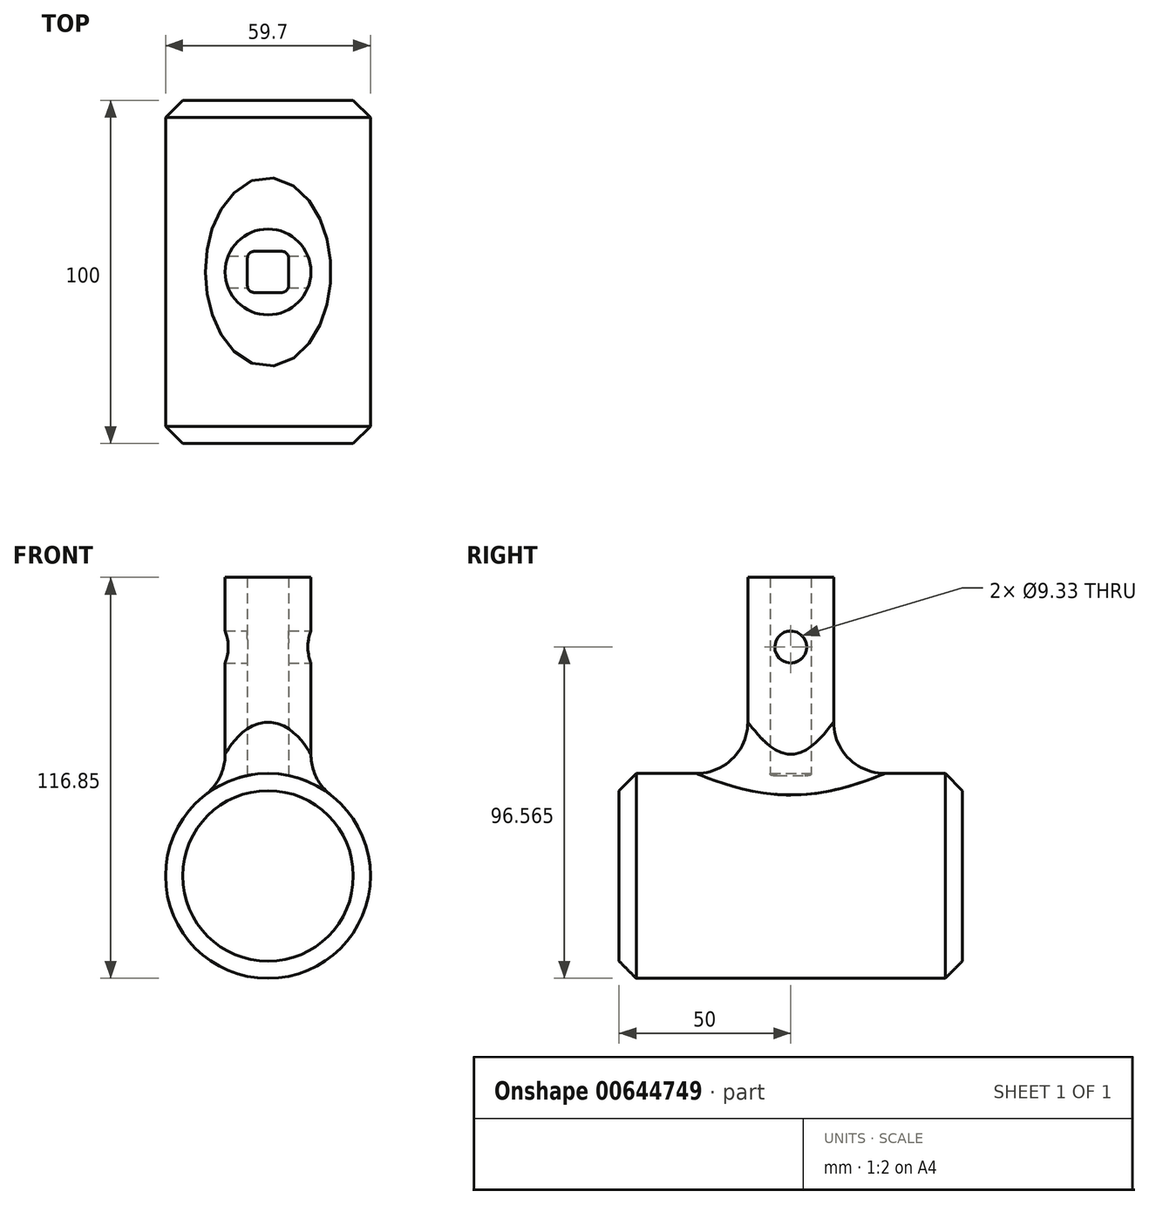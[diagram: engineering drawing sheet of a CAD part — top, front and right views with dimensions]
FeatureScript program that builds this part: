
annotation { "Feature Type Name" : "Feature", "Feature Type Description" : "" }
export const myFeature = defineFeature(function(context is Context, id is Id, definition is map)
    precondition{}
    {
        {
            var Q0;
            Q0=qCreatedBy(makeId("Top.planeOp"),FACE);
            var sketch = newSketch(context, id + "F0", { "sketchPlane" : qUnion([Q0])});
            skCircle(sketch, "E0", {"center": v(0, 0) * mm, "radius": 12.5 * mm});
            skLineSegment(sketch, "E1.bottom", {"start": v(4, -6) * mm, "end": v(-4, -6) * mm});
            skLineSegment(sketch, "E1.top", {"start": v(4, 6) * mm, "end": v(-4, 6) * mm});
            skLineSegment(sketch, "E1.left", {"start": v(6, -4) * mm, "end": v(6, 4) * mm});
            skLineSegment(sketch, "E1.right", {"start": v(-6, -4) * mm, "end": v(-6, 4) * mm});
            skPoint(sketch, "E2.visualSharp", {"position": v(-6, 6) * mm});
            skArc(sketch, "E2.filletArc", {"start": v(-4, 6) * mm, "mid": v(-5.41, 5.41) * mm, "end": v(-6, 4) * mm});
            skPoint(sketch, "E3.visualSharp", {"position": v(-6, -6) * mm});
            skArc(sketch, "E3.filletArc", {"start": v(-6, -4) * mm, "mid": v(-5.41, -5.41) * mm, "end": v(-4, -6) * mm});
            skPoint(sketch, "E4.visualSharp", {"position": v(6, -6) * mm});
            skArc(sketch, "E4.filletArc", {"start": v(4, -6) * mm, "mid": v(5.41, -5.41) * mm, "end": v(6, -4) * mm});
            skPoint(sketch, "E5.visualSharp", {"position": v(6, 6) * mm});
            skArc(sketch, "E5.filletArc", {"start": v(6, 4) * mm, "mid": v(5.41, 5.41) * mm, "end": v(4, 6) * mm});
            skSolve(sketch);
        }
        {
            var Q0;
            Q0 = qSketchRegion(id + "F0", true);
            extrude(context, id + "F1", {"entities" : qUnion([Q0]), "depth" : 87 * mm, "offsetDistance" : 25 * mm});
        }
        {
            var Q0;
            Q0=qCreatedBy(makeId("Front.planeOp"),FACE);
            var sketch = newSketch(context, id + "F2", { "sketchPlane" : qUnion([Q0])});
            skCircle(sketch, "E6", {"center": v(0, 0) * mm, "radius": 29.85 * mm});
            skSolve(sketch);
        }
        {
            var Q0;
            Q0 = qSketchRegion(id + "F2", true);
            extrude(context, id + "F3", {"entities" : qUnion([Q0]), "operationType" : NewBodyOperationType.ADD, "endBound" : BoundingType.SYMMETRIC, "depth" : 100 * mm, "offsetDistance" : 25 * mm});
        }
        {
            var Q0;
            Q0=makeQuery(id+"F3.boolean.opBoolean","INTERSECT",EDGE,{"derivedFrom":[makeQuery(id+"F1.opExtrude","SWEPT_FACE",FACE,{"disambiguationData":[OSD([sQuery(id+"F0.wireOp",EDGE,"E0")])]}),makeQuery(id+"F3.opExtrude","SWEPT_FACE",FACE,{"disambiguationData":[OSD([sQuery(id+"F2.wireOp",EDGE,"E6")])]})]});
            fillet(context, id + "F4", {"entities" : qUnion([Q0]), "radius" : 15 * mm, "tangentPropagation" : true, "allowEdgeOverflow" : false});
        }
        {
            var Q0;
            Q0=makeQuery(id+"F3.opExtrude","CAP_EDGE",EDGE,{"disambiguationData":[OSD([sQuery(id+"F2.wireOp",EDGE,"E6")])],"isStart":true});
            var Q1;
            Q1=makeQuery(id+"F3.opExtrude","CAP_EDGE",EDGE,{"disambiguationData":[OSD([sQuery(id+"F2.wireOp",EDGE,"E6")])],"isStart":false});
            chamfer(context, id + "F5", {"entities" : qUnion([Q0, Q1]), "width" : 5 * mm, "tangentPropagation" : true});
        }
        {
            var Q0;
            Q0=qCreatedBy(makeId("Right.planeOp"),FACE);
            var sketch = newSketch(context, id + "F6", { "sketchPlane" : qUnion([Q0])});
            skCircle(sketch, "E7", {"center": v(0, 66.72) * mm, "radius": 4.66 * mm});
            skSolve(sketch);
        }
        {
            var Q0;
            Q0 = qSketchRegion(id + "F6", true);
            extrude(context, id + "F7", {"entities" : qUnion([Q0]), "operationType" : NewBodyOperationType.REMOVE, "endBound" : BoundingType.SYMMETRIC, "oppositeDirection" : true, "depth" : 35 * mm, "offsetDistance" : 25 * mm});
        }
    });
